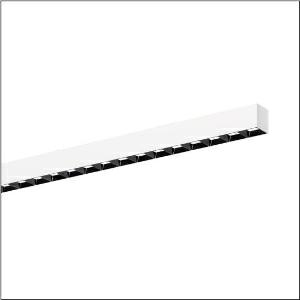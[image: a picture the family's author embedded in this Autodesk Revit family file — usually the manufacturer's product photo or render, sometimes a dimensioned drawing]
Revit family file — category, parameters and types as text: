
# Revit family: silica_r__21_51mx24tbt5w_c5f4
name_source: partatom
category: Lighting Fixtures
units: mm (PartAtom-declared; Revit-internal decimal feet)

## family parameters
Cut with Voids When Loaded = No
Host = Face
Light Source = No
Part Type = Normal
Room Calculation Point = No
Round Connector Dimension = Use Diameter
Shared = No

## types (1)
- --- (1 x LED, 4100 lm, 40.5 W, 6500K)
    Apparent Load = 41 VA
    CIE Flux Codes = 74 94 99 100 100
    Color Rendering = 80
    Color Temperature = 6500K
    Default Elevation = 1800 mm
    Description = Silica® 21, office luminaire, primary light control with darklight reflector, of PMMA, black, light emission: direct distribution, primary light characteristic: asymmetric, installation type: surface-mounted, LED, rated luminous flux: 4.100lm, luminous efficacy: 96lm/W, light colour: 8tw, colour temperature: 2700..6500K, control gear: ECG DALI, with terminal, 3+2-pole, max. 2.5mm², mains connection: 220..240V, AC, 50/60Hz, rated input power: 42.6W, luminaire housing, of aluminium, traffic white (RAL 9016), length: 1.504mm, width: 53mm, height: 53mm, protection rating (complete): IP20, insulation class (complete): insulation class I (protective earthing), certification: CE, permissible operating ambient temperature: 0..+35°C, standard: EN 50419, packaging unit: 1 piece
    Height = 0 mm  [stored 0 ft]
    Lamp = 1 x LED
    Lamp Light Flux = 4100 lm
    Lamp Power = 40.5 W
    Lamp count = 1
    Length = 1504 mm
    Luminous efficacy = 101 lm/W
    Manufacturer = Siteco
    ModVariant = No
    Model = 51MX24TBT5W
    Mounting Place = Ceiling
    Mounting Type = Recessed
    Number of Poles = 1
    OnlyDefault = Yes
    Power Factor = 1
    Product Name = Silica® 21
    Product group = office luminaire | ceiling recessed
    ProductGroupID = 401
    Protection Class = Protection class I
    Protection Degree = IP 20
    RLX_Detail_Level = 1
    RLX_Emergency_Light_Flux = 0 lm
    RLX_Emergency_Type = 0
    RLX_Emergency_Type_DB = No
    RlxData = <blob elided: 41881 chars, md5=5fab3be8>
    Socket = socket
    Standby Power = 0 W
    System Light Flux = 4100 lm
    System Power = 41 W
    Type Comments = individual setting
    Type Image = l_1297779.jpg
    URL = http://relux.com
    VarID = @adj_071335
    Voltage = 0 V
    Weight = 0.00 kg
    Width = 53 mm

note: [stored X ft] marks values corroborated as IEEE doubles in the binary element streams (Revit-internal decimal feet)

## geometry (parser evidence)
native form markers: Blend x4, Sweep x8
no freeform markers — native parametric forms only
